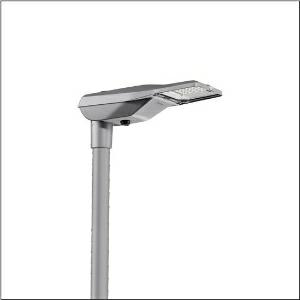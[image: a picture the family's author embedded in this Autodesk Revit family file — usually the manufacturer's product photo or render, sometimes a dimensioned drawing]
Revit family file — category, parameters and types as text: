
# Revit family: streetlight_sl_21_iq_micro___p0_5a_5xe1v31u08db_ec29
name_source: partatom
category: Lighting Fixtures
units: mm (PartAtom-declared; Revit-internal decimal feet)

## family parameters
Cut with Voids When Loaded = No
Host = Face
Light Source = No
Part Type = Normal
Room Calculation Point = No
Round Connector Dimension = Use Diameter
Shared = No

## types (1)
- --- (1 x LED, 5030 lm, 39.1 W, 3000K)
    Apparent Load = 39 VA
    CIE Flux Codes = 37 73 96 100 100
    Color Rendering = 70
    Color Temperature = 3000K
    Default Elevation = 1800 mm
    Description = Streetlight SL 21 iQ micro, mast luminaire, primary light control with lens, of PMMA, primary optical cover: cover, of toughened safety glass, transparent, light distribution: P0.5a, light emission: direct distribution, primary light characteristic: asymmetric, installation type: post-top, side-entry, LED, High Power LED, rated luminous flux: 5.030lm, luminous efficacy: 129lm/W, light colour: 730, colour temperature: 3000K, control gear: iQ-Street Remote, D4i with power reduction, control: pre-setting: logarithmic dimming characteristic, Street-Remote, Auto-Match, Temp-Guard, Lumen-Switch, Night-Set, Smart-Wire, Light-Fading, Desk-Remote (wireless, voltage-free reading and setting of iQ features in the workshop via application-optimized NFC function/RFID function), optimised constant luminous flux control (CLO 2.0), mains connection: 220..240V, AC, 50/60Hz, start of lifetime: 39W, end of service life: 41W, reduction: 17W, luminaire housing, of diecast aluminium, powder-coated, SITECO metallic grey (DB 702S), corrosivity category C5 high according to DIN EN ISO 12944, please order mast flange separately, inclination adjustable: 0°, 5°, 10°, 15°, sealing non-destructively replaceable, multi-level sealing system, length: 528mm, width: 235mm, height: 110mm, mast flange for spigot size: 42mm (side-entry): 5XC10008XM4, 60/48mm (side-entry/post-top): 5XC10108XM2, 76/60mm (side-entry/post-top): 5XC10108XM1, mounting height: 4..8m, Smart Interface below, protection rating (complete): IP66, insulation class (complete): insulation class II (safety insulation), certification: CE, ENEC, ENEC+, VDE, impact resistance: IK10, permissible operating ambient temperature for outdoor applications: -40..+50°C, standard-compliant lighting for roads and squares, packaging unit: 1 piece

Light Distribution: P0.5a
    Height = 110 mm
    Lamp = 1 x LED
    Lamp Light Flux = 5030 lm
    Lamp Power = 39.1 W
    Lamp count = 1
    Length = 528 mm
    Luminous efficacy = 129 lm/W
    Manufacturer = Siteco
    ModVariant = No
    Model = 5XE1V31U08DB
    Number of Poles = 1
    OnlyDefault = Yes
    Power Factor = 1
    Product Name = Streetlight SL 21 iQ micro | P0.5a
    Product group = mast luminaire | pylon top
    ProductGroupID = 6100
    Protection Class = Protection class II
    Protection Degree = IP 66
    RLX_Detail_Level = 1
    RLX_Emergency_Light_Flux = 0 lm
    RLX_Emergency_Type = 0
    RLX_Emergency_Type_DB = No
    RlxData = <blob elided: 98397 chars, md5=a01b90d1>
    Socket = socket
    Standby Power = 0 W
    System Light Flux = 5030 lm
    System Power = 39 W
    Type Comments = factory setting: luminous flux: 100 % | dim-lin: 254 | 765 mA
    Type Image = l_1277290.jpg
    URL = http://relux.com
    VarID = @adj_078607
    Voltage = 0 V
    Weight = 0.00 kg
    Width = 235 mm

## geometry (parser evidence)
native form markers: Blend x4, Sweep x12
no freeform markers — native parametric forms only
